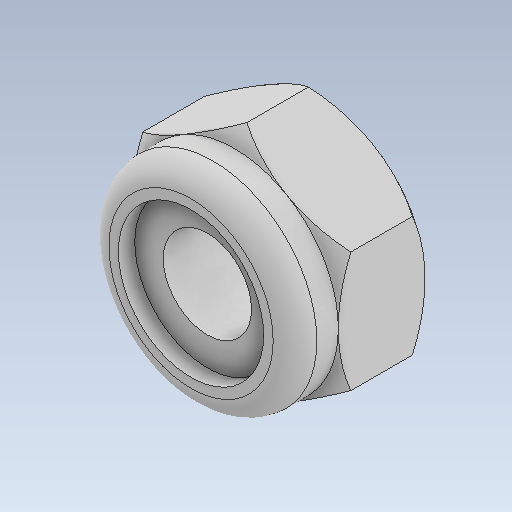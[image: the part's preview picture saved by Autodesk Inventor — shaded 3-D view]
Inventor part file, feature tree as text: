
AUTODESK INVENTOR PART (.ipt)
format: ipt  version: 2020.2 (Build 242310000, 310)  size: 161,792 bytes
history: native  units: in
note: dims shown in document units (in); Inventor stores cm internally (conversion verified against a paired STEP export)
features: fillet x1
ambient origin geometry x8: Origin, YZ Plane, XZ Plane, XY Plane, X Axis, Y Axis, Z Axis, Center Point
bodies: Solid1 (feature_tree)
feature tree (1):
  fillet  "Fillet1"  [1 undecoded]
note: 1 required parameter value undecoded (feature->parameter linkage not recoverable at this tier; creation-order binding heuristic only, values carry confidence <= 0.55)
